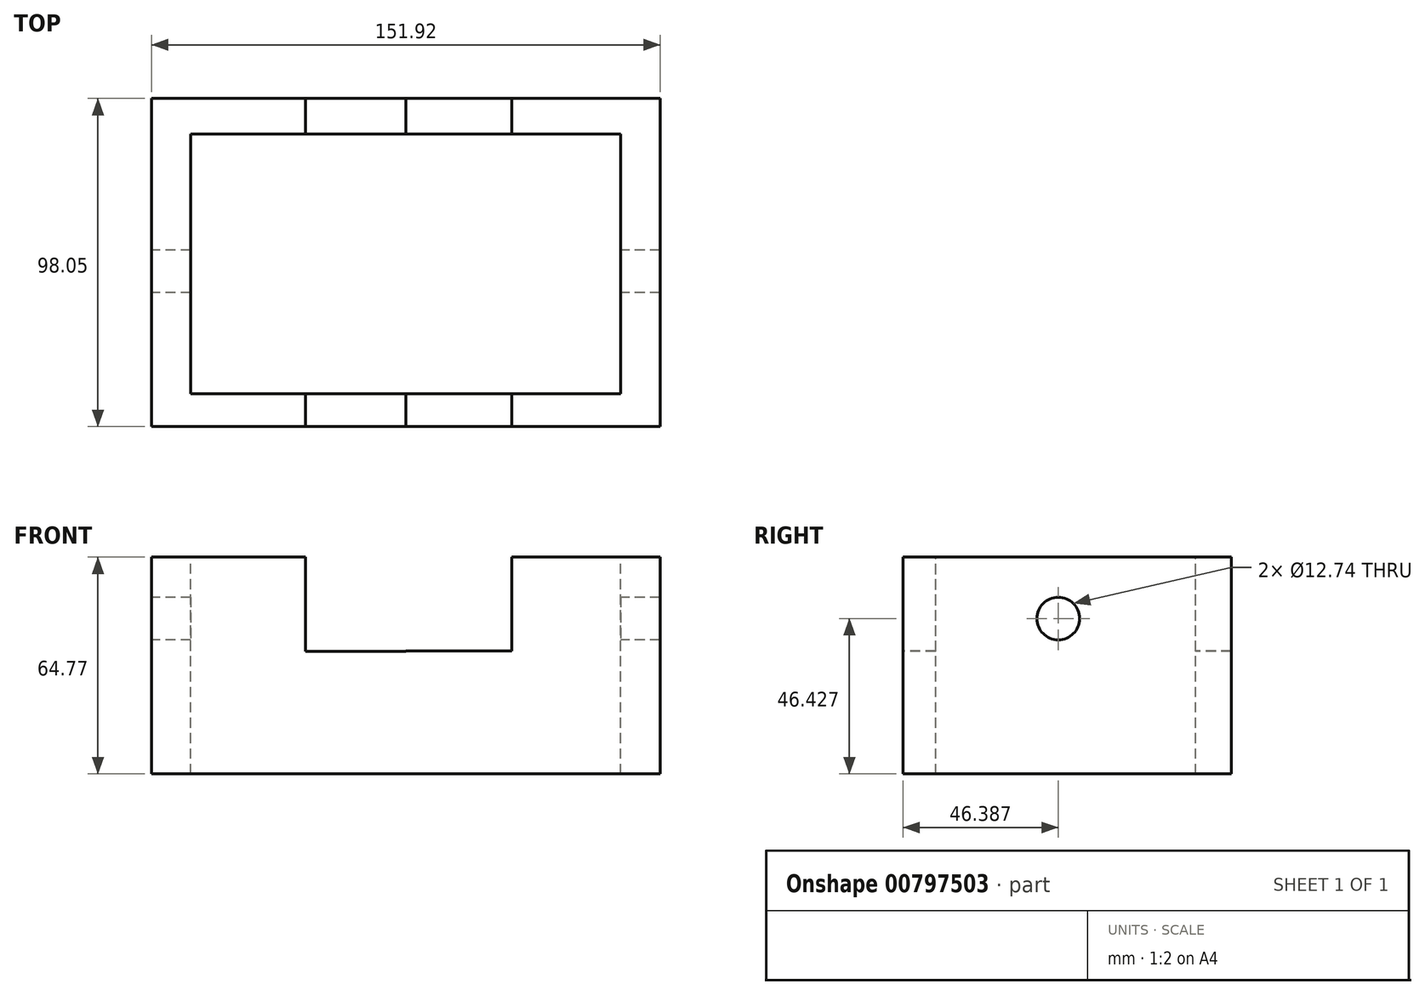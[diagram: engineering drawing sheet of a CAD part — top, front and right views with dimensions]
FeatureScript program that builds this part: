
annotation { "Feature Type Name" : "Feature", "Feature Type Description" : "" }
export const myFeature = defineFeature(function(context is Context, id is Id, definition is map)
    precondition{}
    {
        {
            var Q0;
            Q0=qCreatedBy(makeId("Top.planeOp"),FACE);
            var sketch = newSketch(context, id + "F0", { "sketchPlane" : qUnion([Q0])});
            skLineSegment(sketch, "E0.bottom", {"start": v(75.96, 56.14) * mm, "end": v(-75.96, 56.14) * mm});
            skLineSegment(sketch, "E0.top", {"start": v(75.96, -56.14) * mm, "end": v(-75.96, -56.14) * mm});
            skLineSegment(sketch, "E0.left", {"start": v(75.96, 56.14) * mm, "end": v(75.96, -56.14) * mm});
            skLineSegment(sketch, "E0.right", {"start": v(-75.96, 56.14) * mm, "end": v(-75.96, -56.14) * mm});
            skPoint(sketch, "E0.middle", {"position": v(0, 0) * mm});
            skSolve(sketch);
        }
        {
            var Q0;
            Q0=makeQuery(id+"F0.imprint","IMPRINT",FACE,{"disambiguationData":[TD([[makeQuery(id+"F0.imprint","IMPRINT",EDGE,{"derivedFrom":sQuery(id+"F0.wireOp",EDGE,"E0.bottom")}),1.0]])]});
            extrude(context, id + "F1", {"entities" : qUnion([Q0]), "depth" : 64.77 * mm, "offsetDistance" : 25.4 * mm});
        }
        {
            var Q0;
            Q0=makeQuery(id+"F1.opExtrude","SWEPT_FACE",FACE,{"disambiguationData":[OSD([sQuery(id+"F0.wireOp",EDGE,"E0.top")])]});
            var sketch = newSketch(context, id + "F2", { "sketchPlane" : qUnion([Q0])});
            skLineSegment(sketch, "E1.bottom", {"start": v(0, 64.77) * mm, "end": v(-33.72, 64.77) * mm});
            skLineSegment(sketch, "E1.top", {"start": v(0, 40.93) * mm, "end": v(-33.72, 40.93) * mm});
            skLineSegment(sketch, "E1.left", {"start": v(0, 64.77) * mm, "end": v(0, 40.93) * mm});
            skLineSegment(sketch, "E1.right", {"start": v(-33.72, 64.77) * mm, "end": v(-33.72, 40.93) * mm});
            skLineSegment(sketch, "E2.bottom", {"start": v(0, 64.77) * mm, "end": v(34.93, 64.77) * mm});
            skLineSegment(sketch, "E2.top", {"start": v(0, 40.93) * mm, "end": v(34.93, 40.93) * mm});
            skLineSegment(sketch, "E2.right", {"start": v(34.93, 64.77) * mm, "end": v(34.93, 40.93) * mm});
            skSolve(sketch);
        }
        {
            var Q0;
            Q0=makeQuery(id+"F1.opExtrude","CAP_FACE",FACE,{"disambiguationData":[OSD([sQuery(id+"F0.wireOp",EDGE,"E0.bottom"),sQuery(id+"F0.wireOp",EDGE,"E0.top"),sQuery(id+"F0.wireOp",EDGE,"E0.left"),sQuery(id+"F0.wireOp",EDGE,"E0.right")])],"isStart":false});
            var sketch = newSketch(context, id + "F3", { "sketchPlane" : qUnion([Q0])});
            skLineSegment(sketch, "E3.bottom", {"start": v(64.2, 45.53) * mm, "end": v(-64.2, 45.53) * mm});
            skLineSegment(sketch, "E3.top", {"start": v(64.2, -32.15) * mm, "end": v(-64.2, -32.15) * mm});
            skLineSegment(sketch, "E3.left", {"start": v(64.2, 45.53) * mm, "end": v(64.2, -32.15) * mm});
            skLineSegment(sketch, "E3.right", {"start": v(-64.2, 45.53) * mm, "end": v(-64.2, -32.15) * mm});
            skPoint(sketch, "E3.middle", {"position": v(0, 6.7) * mm});
            skSolve(sketch);
        }
        {
            var Q0;
            Q0=makeQuery(id+"F2.imprint","IMPRINT",FACE,{"disambiguationData":[TD([[makeQuery(id+"F2.imprint","IMPRINT",EDGE,{"derivedFrom":sQuery(id+"F2.wireOp",EDGE,"E1.top")}),1.0]])]});
            var Q1;
            Q1=makeQuery(id+"F2.imprint","IMPRINT",FACE,{"disambiguationData":[TD([[makeQuery(id+"F2.imprint","IMPRINT",EDGE,{"derivedFrom":sQuery(id+"F2.wireOp",EDGE,"E1.bottom")}),1.0]])]});
            var Q2;
            Q2=makeQuery(id+"F2.imprint","IMPRINT",FACE,{"disambiguationData":[TD([[makeQuery(id+"F2.imprint","IMPRINT",EDGE,{"derivedFrom":sQuery(id+"F2.wireOp",EDGE,"E2.bottom")}),1.0]])]});
            extrude(context, id + "F4", {"entities" : qUnion([Q0, Q1, Q2]), "operationType" : NewBodyOperationType.REMOVE, "oppositeDirection" : true, "depth" : 14.22 * mm, "offsetDistance" : 25.4 * mm});
        }
        {
            var Q0;
            Q0=makeQuery(id+"F3.imprint","IMPRINT",FACE,{"disambiguationData":[TD([[makeQuery(id+"F3.imprint","IMPRINT",EDGE,{"derivedFrom":sQuery(id+"F3.wireOp",EDGE,"E3.bottom")}),1.0]])]});
            extrude(context, id + "F5", {"entities" : qUnion([Q0]), "operationType" : NewBodyOperationType.REMOVE, "oppositeDirection" : true, "depth" : 191.52 * mm, "offsetDistance" : 25.4 * mm});
        }
        {
            var Q0;
            Q0=makeQuery(id+"F4.boolean.opBoolean","COPY",FACE,{"derivedFrom":makeQuery(id+"F4.opExtrude","CAP_FACE",FACE,{"disambiguationData":[OSD([sQuery(id+"F0.wireOp",EDGE,"E0.top"),sQuery(id+"F0.wireOp",EDGE,"E0.left"),sQuery(id+"F0.wireOp",EDGE,"E0.right"),sQuery(id+"F2.wireOp",EDGE,"E1.bottom"),sQuery(id+"F2.wireOp",EDGE,"E2.bottom")])],"isStart":false})});
            var sketch = newSketch(context, id + "F6", { "sketchPlane" : qUnion([Q0])});
            skLineSegment(sketch, "E4.bottom", {"start": v(0, 64.77) * mm, "end": v(-30.02, 64.77) * mm});
            skLineSegment(sketch, "E4.top", {"start": v(0, 36.58) * mm, "end": v(-30.02, 36.58) * mm});
            skLineSegment(sketch, "E4.left", {"start": v(0, 64.77) * mm, "end": v(0, 36.58) * mm});
            skLineSegment(sketch, "E4.right", {"start": v(-30.02, 64.77) * mm, "end": v(-30.02, 36.58) * mm});
            skLineSegment(sketch, "E5.bottom", {"start": v(0, 64.77) * mm, "end": v(31.64, 64.77) * mm});
            skLineSegment(sketch, "E5.top", {"start": v(0, 36.72) * mm, "end": v(31.64, 36.72) * mm});
            skLineSegment(sketch, "E5.left", {"start": v(0, 64.77) * mm, "end": v(0, 36.72) * mm});
            skLineSegment(sketch, "E5.right", {"start": v(31.64, 64.77) * mm, "end": v(31.64, 36.72) * mm});
            skSolve(sketch);
        }
        {
            var Q0;
            Q0=makeQuery(id+"F6.imprint","IMPRINT",FACE,{"disambiguationData":[TD([[makeQuery(id+"F6.imprint","IMPRINT",EDGE,{"derivedFrom":sQuery(id+"F6.wireOp",EDGE,"E4.bottom")}),1.0]])]});
            var Q1;
            Q1=makeQuery(id+"F6.imprint","IMPRINT",FACE,{"disambiguationData":[TD([[makeQuery(id+"F6.imprint","IMPRINT",EDGE,{"derivedFrom":sQuery(id+"F6.wireOp",EDGE,"E5.bottom")}),1.0]])]});
            extrude(context, id + "F7", {"entities" : qUnion([Q0, Q1]), "operationType" : NewBodyOperationType.REMOVE, "oppositeDirection" : true, "depth" : 367.03 * mm, "offsetDistance" : 25.4 * mm});
        }
        {
            var Q0;
            Q0=makeQuery(id+"F1.opExtrude","SWEPT_FACE",FACE,{"disambiguationData":[OSD([sQuery(id+"F0.wireOp",EDGE,"E0.right")])]});
            var sketch = newSketch(context, id + "F8", { "sketchPlane" : qUnion([Q0])});
            skCircle(sketch, "E6", {"center": v(-4.48, 46.43) * mm, "radius": 6.37 * mm});
            skSolve(sketch);
        }
        {
            var Q0;
            Q0=makeQuery(id+"F8.imprint","IMPRINT",FACE,{"disambiguationData":[TD([[makeQuery(id+"F8.imprint","IMPRINT",EDGE,{"derivedFrom":sQuery(id+"F8.wireOp",EDGE,"E6")}),1.0]])]});
            extrude(context, id + "F9", {"entities" : qUnion([Q0]), "operationType" : NewBodyOperationType.REMOVE, "oppositeDirection" : true, "depth" : 199.39 * mm, "offsetDistance" : 25.4 * mm});
        }
    });
